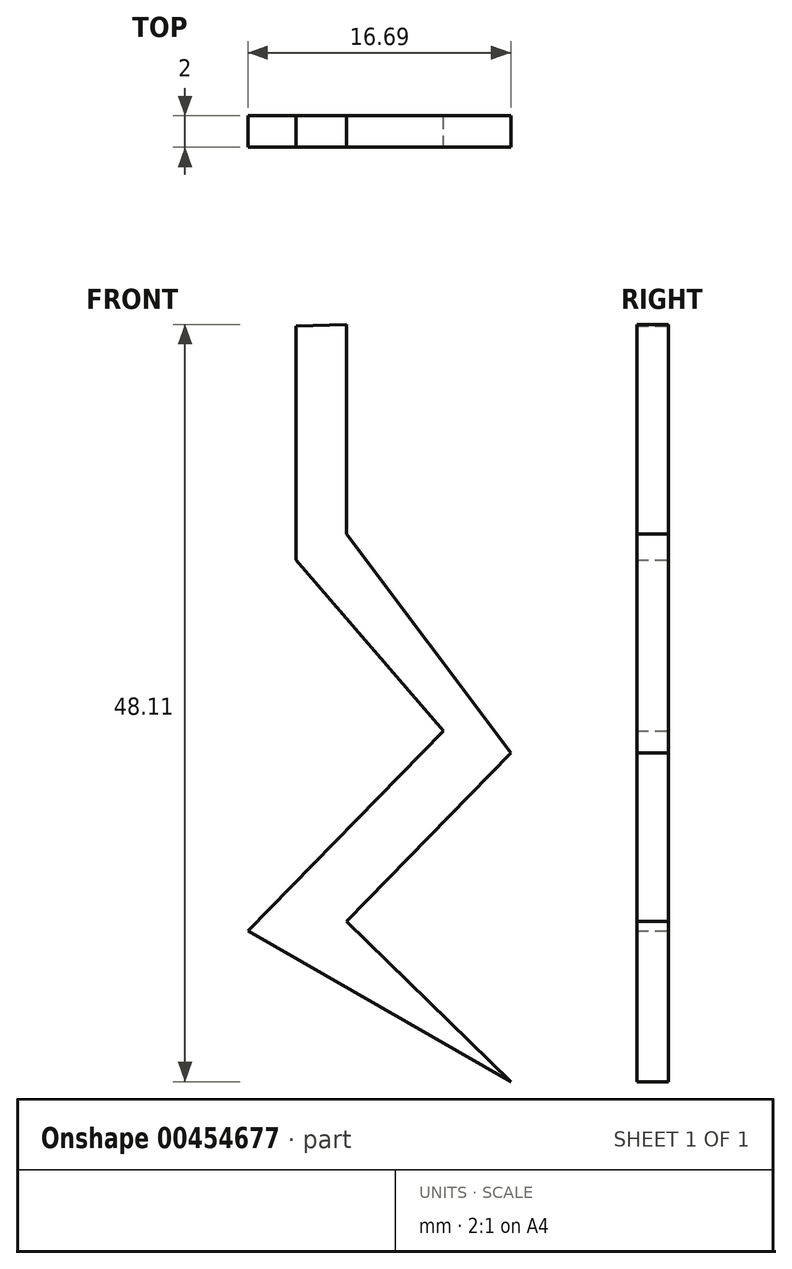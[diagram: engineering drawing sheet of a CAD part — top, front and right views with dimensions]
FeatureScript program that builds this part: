
annotation { "Feature Type Name" : "Feature", "Feature Type Description" : "" }
export const myFeature = defineFeature(function(context is Context, id is Id, definition is map)
    precondition{}
    {
        {
            var Q0;
            Q0=qCreatedBy(makeId("Front.planeOp"),FACE);
            var sketch = newSketch(context, id + "F0", { "sketchPlane" : qUnion([Q0])});
            skLineSegment(sketch, "E0", {"start": v(0, 0) * mm, "end": v(-16.69, 9.57) * mm});
            skLineSegment(sketch, "E1", {"start": v(-16.69, 9.57) * mm, "end": v(-4.29, 22.28) * mm});
            skLineSegment(sketch, "E2", {"start": v(-4.29, 22.28) * mm, "end": v(-13.63, 33.15) * mm});
            skLineSegment(sketch, "E3", {"start": v(-13.63, 33.15) * mm, "end": v(-13.63, 48) * mm});
            skLineSegment(sketch, "E4", {"start": v(0, 0) * mm, "end": v(-10.44, 10.18) * mm});
            skLineSegment(sketch, "E5", {"start": v(-10.44, 10.18) * mm, "end": v(0, 20.88) * mm});
            skLineSegment(sketch, "E6", {"start": v(0, 20.88) * mm, "end": v(-10.44, 34.8) * mm});
            skLineSegment(sketch, "E7", {"start": v(-10.44, 34.8) * mm, "end": v(-10.44, 48.1) * mm});
            skLineSegment(sketch, "E8", {"start": v(-10.44, 48.1) * mm, "end": v(-13.63, 48) * mm});
            skSolve(sketch);
        }
        {
            var Q0;
            Q0 = qSketchRegion(id + "F0", true);
            extrude(context, id + "F1", {"entities" : qUnion([Q0]), "depth" : 2 * mm, "offsetDistance" : 25 * mm});
        }
    });
